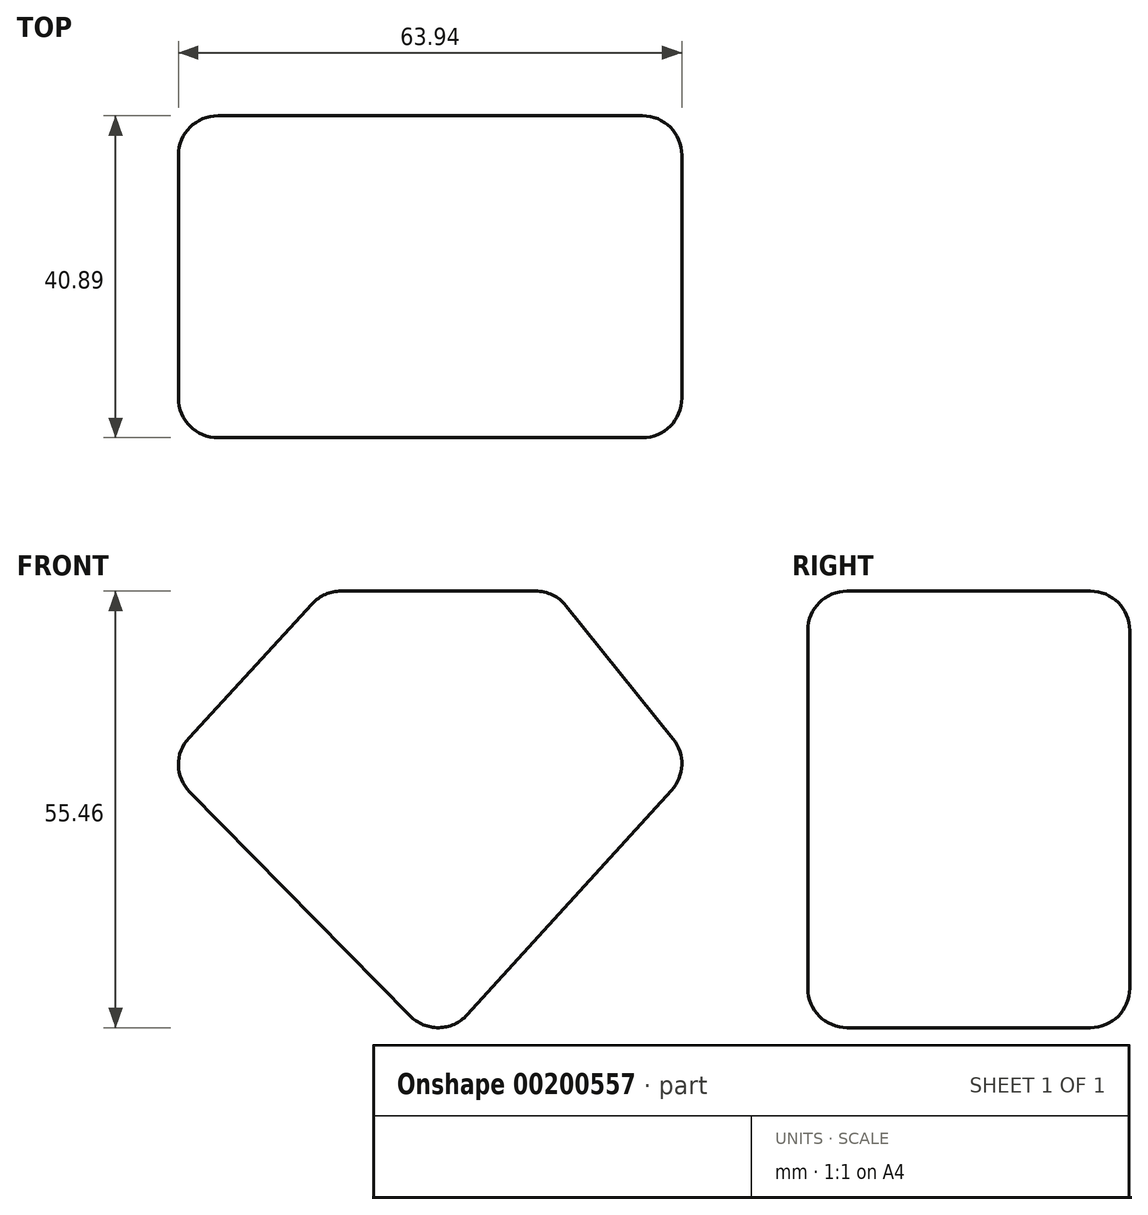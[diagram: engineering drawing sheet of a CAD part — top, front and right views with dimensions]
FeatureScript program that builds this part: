
annotation { "Feature Type Name" : "Feature", "Feature Type Description" : "" }
export const myFeature = defineFeature(function(context is Context, id is Id, definition is map)
    precondition{}
    {
        {
            var Q0;
            Q0=qCreatedBy(makeId("Front.planeOp"),FACE);
            var sketch = newSketch(context, id + "F0", { "sketchPlane" : qUnion([Q0])});
            skLineSegment(sketch, "E0", {"start": v(2.1, 0) * mm, "end": v(22.48, 22.13) * mm});
            skLineSegment(sketch, "E1", {"start": v(22.48, 22.13) * mm, "end": v(51.74, 22.13) * mm});
            skLineSegment(sketch, "E2", {"start": v(51.74, 22.13) * mm, "end": v(69.51, 0) * mm});
            skLineSegment(sketch, "E3", {"start": v(69.51, 0) * mm, "end": v(37.11, -35.6) * mm});
            skLineSegment(sketch, "E4", {"start": v(37.11, -35.6) * mm, "end": v(2.1, 0) * mm});
            skSolve(sketch);
        }
        {
            var Q0;
            Q0=makeQuery(id+"F0.imprint","IMPRINT",FACE,{"disambiguationData":[TD([[makeQuery(id+"F0.imprint","IMPRINT",EDGE,{"derivedFrom":sQuery(id+"F0.wireOp",EDGE,"E0")}),-1.0]])]});
            extrude(context, id + "F1", {"entities" : qUnion([Q0]), "depth" : 40.9 * mm});
        }
        {
            var Q0;
            Q0=makeQuery(id+"F1.opExtrude","SWEPT_FACE",FACE,{"disambiguationData":[OSD([sQuery(id+"F0.wireOp",EDGE,"E2")])]});
            var Q1;
            Q1=makeQuery(id+"F1.opExtrude","CAP_FACE",FACE,{"disambiguationData":[OSD([sQuery(id+"F0.wireOp",EDGE,"E0"),sQuery(id+"F0.wireOp",EDGE,"E1"),sQuery(id+"F0.wireOp",EDGE,"E2"),sQuery(id+"F0.wireOp",EDGE,"E3"),sQuery(id+"F0.wireOp",EDGE,"E4")])],"isStart":false});
            var Q2;
            Q2=makeQuery(id+"F1.opExtrude","SWEPT_FACE",FACE,{"disambiguationData":[OSD([sQuery(id+"F0.wireOp",EDGE,"E1")])]});
            var Q3;
            Q3=makeQuery(id+"F1.opExtrude","SWEPT_FACE",FACE,{"disambiguationData":[OSD([sQuery(id+"F0.wireOp",EDGE,"E0")])]});
            var Q4;
            Q4=makeQuery(id+"F1.opExtrude","SWEPT_FACE",FACE,{"disambiguationData":[OSD([sQuery(id+"F0.wireOp",EDGE,"E4")])]});
            var Q5;
            Q5=makeQuery(id+"F1.opExtrude","CAP_EDGE",EDGE,{"disambiguationData":[OSD([sQuery(id+"F0.wireOp",EDGE,"E3")])],"isStart":false});
            var Q6;
            Q6=makeQuery(id+"F1.opExtrude","SWEPT_FACE",FACE,{"disambiguationData":[OSD([sQuery(id+"F0.wireOp",EDGE,"E3")])]});
            var Q7;
            Q7=makeQuery(id+"F1.opExtrude","CAP_FACE",FACE,{"disambiguationData":[OSD([sQuery(id+"F0.wireOp",EDGE,"E0"),sQuery(id+"F0.wireOp",EDGE,"E1"),sQuery(id+"F0.wireOp",EDGE,"E2"),sQuery(id+"F0.wireOp",EDGE,"E3"),sQuery(id+"F0.wireOp",EDGE,"E4")])],"isStart":true});
            var Q8;
            Q8=makeQuery(id+"F1.opExtrude","CAP_EDGE",EDGE,{"disambiguationData":[OSD([sQuery(id+"F0.wireOp",EDGE,"E2")])],"isStart":false});
            fillet(context, id + "F2", {"entities" : qUnion([Q0, Q1, Q2, Q3, Q4, Q5, Q6, Q7, Q8]), "radius" : 5 * mm, "tangentPropagation" : true, "allowEdgeOverflow" : false});
        }
    });
